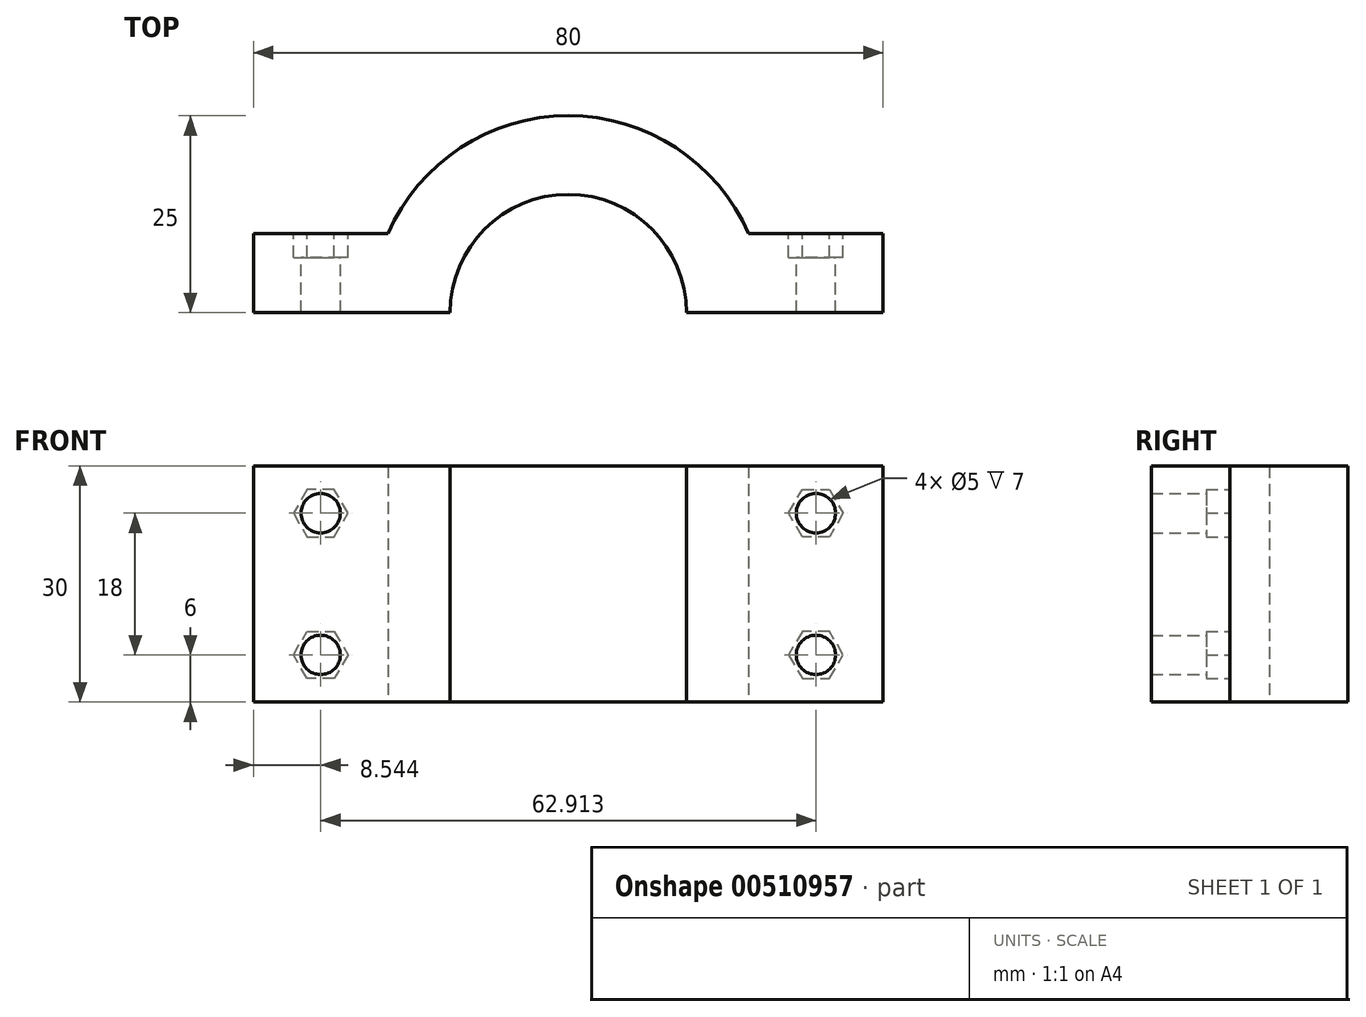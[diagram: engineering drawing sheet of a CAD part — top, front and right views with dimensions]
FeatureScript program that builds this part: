
annotation { "Feature Type Name" : "Feature", "Feature Type Description" : "" }
export const myFeature = defineFeature(function(context is Context, id is Id, definition is map)
    precondition{}
    {
        {
            var Q0;
            Q0=qCreatedBy(makeId("Top.planeOp"),FACE);
            var sketch = newSketch(context, id + "F0", { "sketchPlane" : qUnion([Q0])});
            skArc(sketch, "E0", {"start": v(15, 0) * mm, "mid": v(0, 15) * mm, "end": v(-15, 0) * mm});
            skArc(sketch, "E1.0", {"start": v(22.91, 10) * mm, "mid": v(0, 25) * mm, "end": v(-22.91, 10) * mm});
            skLineSegment(sketch, "E2", {"start": v(-22.91, 10) * mm, "end": v(-40, 10) * mm});
            skLineSegment(sketch, "E3", {"start": v(-40, 10) * mm, "end": v(-40, 0) * mm});
            skLineSegment(sketch, "E4", {"start": v(40, 0) * mm, "end": v(40, 10) * mm});
            skLineSegment(sketch, "E5", {"start": v(40, 10) * mm, "end": v(22.91, 10) * mm});
            skLineSegment(sketch, "E6", {"start": v(-40, 0) * mm, "end": v(-15, 0) * mm});
            skLineSegment(sketch, "E7", {"start": v(15, 0) * mm, "end": v(40, 0) * mm});
            skSolve(sketch);
        }
        {
            var Q0;
            Q0 = qSketchRegion(id + "F0", true);
            extrude(context, id + "F1", {"entities" : qUnion([Q0]), "endBound" : BoundingType.SYMMETRIC, "depth" : 30 * mm});
        }
        {
            var Q0;
            Q0=makeQuery(id+"F1.opExtrude","SWEPT_FACE",FACE,{"disambiguationData":[OSD([sQuery(id+"F0.wireOp",EDGE,"E5")])]});
            var sketch = newSketch(context, id + "F2", { "sketchPlane" : qUnion([Q0])});
            skCircle(sketch, "E8", {"center": v(-31.46, 9) * mm, "radius": 2.5 * mm});
            skPoint(sketch, "E8.centerSnap0", {"position": v(-31.46, 15) * mm});
            skCircle(sketch, "E9.MirrorC", {"center": v(-31.46, -9) * mm, "radius": 2.5 * mm});
            skCircle(sketch, "E10.MirrorC", {"center": v(31.46, -9) * mm, "radius": 2.5 * mm});
            skCircle(sketch, "E11.MirrorC", {"center": v(31.46, 9) * mm, "radius": 2.5 * mm});
            skSolve(sketch);
        }
        {
            var Q0;
            Q0 = qSketchRegion(id + "F2", true);
            extrude(context, id + "F3", {"entities" : qUnion([Q0]), "operationType" : NewBodyOperationType.REMOVE, "oppositeDirection" : true, "depth" : 15 * mm});
        }
        {
            var Q0;
            Q0=makeQuery(id+"F1.opExtrude","SWEPT_FACE",FACE,{"disambiguationData":[OSD([sQuery(id+"F0.wireOp",EDGE,"E2")])]});
            var sketch = newSketch(context, id + "F4", { "sketchPlane" : qUnion([Q0])});
            skPoint(sketch, "E12.0.midPoint", {"position": v(29.44, 10.48) * mm});
            skCircle(sketch, "E13.cCircle", {"center": v(31.46, 9) * mm, "radius": 3 * mm, "construction": true});
            skLineSegment(sketch, "E13.0", {"start": v(33.19, 6) * mm, "end": v(29.72, 6) * mm});
            skLineSegment(sketch, "E13.1", {"start": v(29.72, 6) * mm, "end": v(28, 9) * mm});
            skLineSegment(sketch, "E13.2", {"start": v(28, 9) * mm, "end": v(29.72, 12) * mm});
            skLineSegment(sketch, "E13.3", {"start": v(29.72, 12) * mm, "end": v(33.19, 12) * mm});
            skLineSegment(sketch, "E13.4", {"start": v(33.19, 12) * mm, "end": v(34.92, 9) * mm});
            skLineSegment(sketch, "E13.5", {"start": v(34.92, 9) * mm, "end": v(33.19, 6) * mm});
            skPoint(sketch, "E13.0.midPoint", {"position": v(31.46, 6) * mm});
            skLineSegment(sketch, "E14.MirrorCS", {"start": v(29.72, -12) * mm, "end": v(33.19, -12) * mm});
            skLineSegment(sketch, "E15.MirrorCS", {"start": v(28, -9) * mm, "end": v(29.72, -12) * mm});
            skLineSegment(sketch, "E16.MirrorCS", {"start": v(33.19, -6) * mm, "end": v(29.72, -6) * mm});
            skCircle(sketch, "E17.MirrorC", {"center": v(31.46, -9) * mm, "radius": 3 * mm, "construction": true});
            skLineSegment(sketch, "E18.MirrorCS", {"start": v(33.19, -12) * mm, "end": v(34.92, -9) * mm});
            skLineSegment(sketch, "E19.MirrorCS", {"start": v(29.72, -6) * mm, "end": v(28, -9) * mm});
            skLineSegment(sketch, "E20.MirrorCS", {"start": v(34.92, -9) * mm, "end": v(33.19, -6) * mm});
            skPoint(sketch, "E21.MirrorP", {"position": v(29.44, -10.48) * mm});
            skPoint(sketch, "E22.MirrorP", {"position": v(31.46, -6) * mm});
            skLineSegment(sketch, "E23.MirrorCS", {"start": v(-34.92, -9) * mm, "end": v(-33.19, -6) * mm});
            skLineSegment(sketch, "E24.MirrorCS", {"start": v(-33.19, 6) * mm, "end": v(-29.72, 6) * mm});
            skLineSegment(sketch, "E25.MirrorCS", {"start": v(-33.19, -6) * mm, "end": v(-29.72, -6) * mm});
            skPoint(sketch, "E26.MirrorP", {"position": v(-31.46, -6) * mm});
            skPoint(sketch, "E27.MirrorP", {"position": v(-29.44, 10.48) * mm});
            skPoint(sketch, "E28.MirrorP", {"position": v(-31.46, 6) * mm});
            skPoint(sketch, "E29.MirrorP", {"position": v(-29.44, -10.48) * mm});
            skLineSegment(sketch, "E30.MirrorCS", {"start": v(-29.72, -6) * mm, "end": v(-28, -9) * mm});
            skLineSegment(sketch, "E31.MirrorCS", {"start": v(-33.19, -12) * mm, "end": v(-34.92, -9) * mm});
            skLineSegment(sketch, "E32.MirrorCS", {"start": v(-29.72, 6) * mm, "end": v(-28, 9) * mm});
            skLineSegment(sketch, "E33.MirrorCS", {"start": v(-28, 9) * mm, "end": v(-29.72, 12) * mm});
            skCircle(sketch, "E34.MirrorC", {"center": v(-31.46, 9) * mm, "radius": 3 * mm, "construction": true});
            skLineSegment(sketch, "E35.MirrorCS", {"start": v(-33.19, 12) * mm, "end": v(-34.92, 9) * mm});
            skLineSegment(sketch, "E36.MirrorCS", {"start": v(-28, -9) * mm, "end": v(-29.72, -12) * mm});
            skLineSegment(sketch, "E37.MirrorCS", {"start": v(-29.72, -12) * mm, "end": v(-33.19, -12) * mm});
            skCircle(sketch, "E38.MirrorC", {"center": v(-31.46, -9) * mm, "radius": 3 * mm, "construction": true});
            skLineSegment(sketch, "E39.MirrorCS", {"start": v(-29.72, 12) * mm, "end": v(-33.19, 12) * mm});
            skLineSegment(sketch, "E40.MirrorCS", {"start": v(-34.92, 9) * mm, "end": v(-33.19, 6) * mm});
            skSolve(sketch);
        }
        {
            var Q0;
            Q0 = qSketchRegion(id + "F4", true);
            extrude(context, id + "F5", {"entities" : qUnion([Q0]), "operationType" : NewBodyOperationType.REMOVE, "oppositeDirection" : true, "depth" : 3 * mm});
        }
    });
